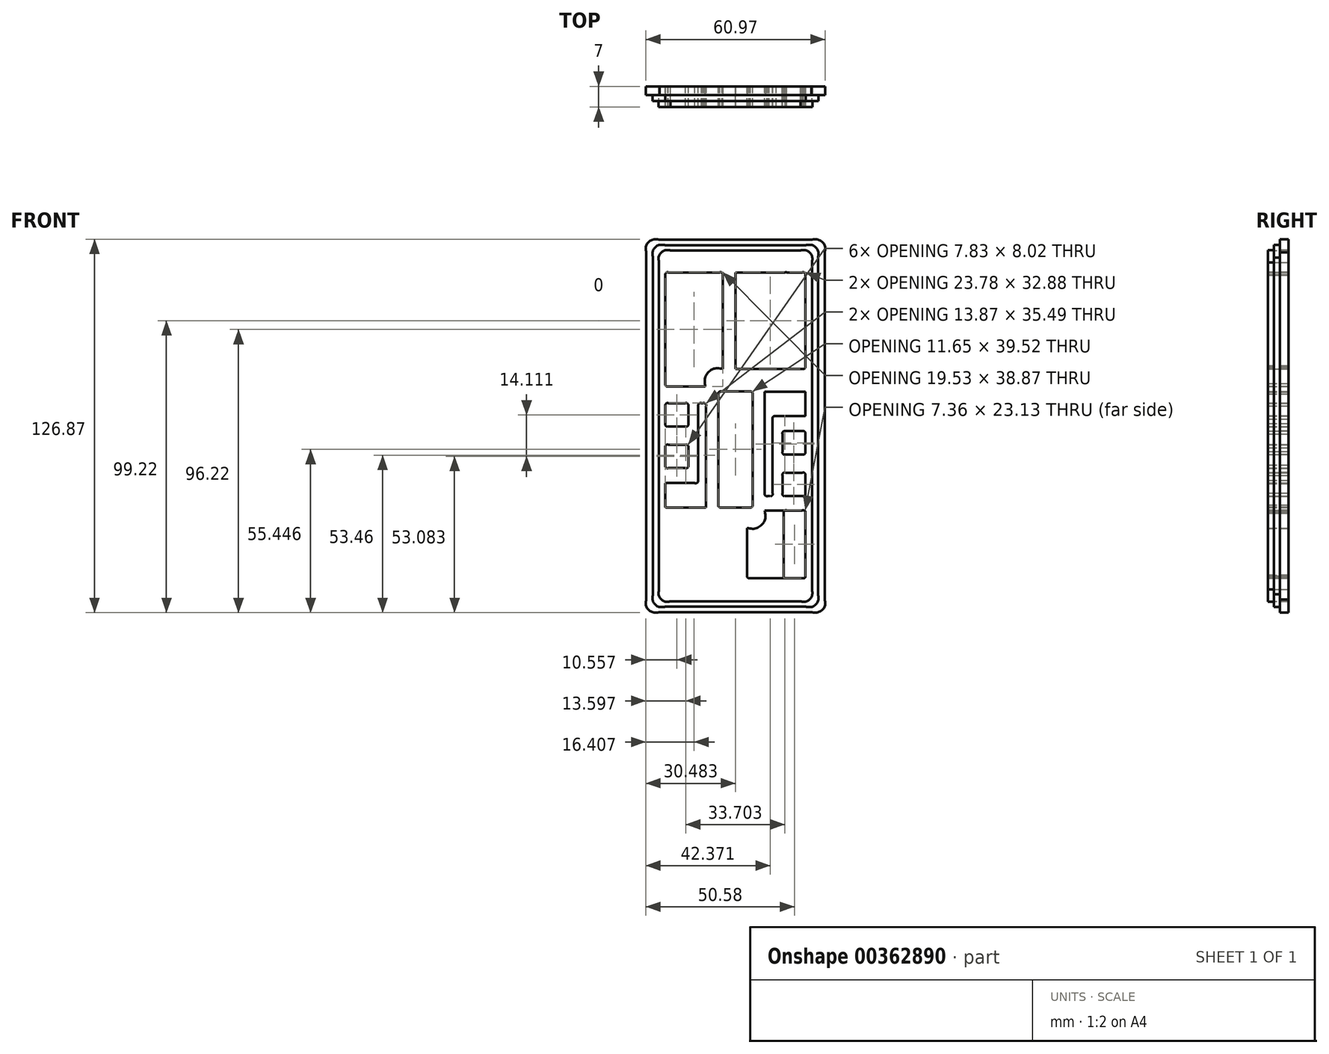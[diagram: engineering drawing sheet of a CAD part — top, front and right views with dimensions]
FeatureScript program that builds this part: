
annotation { "Feature Type Name" : "Feature", "Feature Type Description" : "" }
export const myFeature = defineFeature(function(context is Context, id is Id, definition is map)
    precondition{}
    {
        {
            var Q0;
            Q0=qCreatedBy(makeId("Front.planeOp"),FACE);
            var sketch = newSketch(context, id + "F0", { "sketchPlane" : qUnion([Q0])});
            skFitSpline(sketch, "E0", {"points": [v(-9.5, 11.52) * mm, v(-9.5, 9.28) * mm, v(-11.26, 7.48) * mm, v(-13.43, 7.48) * mm]});
            skFitSpline(sketch, "E1", {"points": [v(-57.55, 7.48) * mm, v(-59.72, 7.48) * mm, v(-61.47, 9.28) * mm, v(-61.47, 11.52) * mm]});
            skLineSegment(sketch, "E2", {"start": v(-13.43, 7.48) * mm, "end": v(-57.55, 7.48) * mm});
            skLineSegment(sketch, "E3", {"start": v(-57.55, 7.48) * mm, "end": v(-13.43, 7.48) * mm});
            skFitSpline(sketch, "E4", {"points": [v(-61.47, 122.72) * mm, v(-61.47, 124.95) * mm, v(-59.72, 126.76) * mm, v(-57.55, 126.76) * mm]});
            skLineSegment(sketch, "E5", {"start": v(-61.47, 11.52) * mm, "end": v(-61.47, 122.72) * mm});
            skLineSegment(sketch, "E6", {"start": v(-61.47, 122.72) * mm, "end": v(-61.47, 11.52) * mm});
            skFitSpline(sketch, "E7", {"points": [v(-13.43, 126.76) * mm, v(-11.26, 126.76) * mm, v(-9.5, 124.95) * mm, v(-9.5, 122.72) * mm]});
            skLineSegment(sketch, "E8", {"start": v(-57.55, 126.76) * mm, "end": v(-13.43, 126.76) * mm});
            skLineSegment(sketch, "E9", {"start": v(-13.43, 126.76) * mm, "end": v(-57.55, 126.76) * mm});
            skFitSpline(sketch, "E10", {"points": [v(-7.42, 9.85) * mm, v(-7.42, 7.55) * mm, v(-9.32, 5.69) * mm, v(-11.66, 5.69) * mm]});
            skLineSegment(sketch, "E11", {"start": v(-9.5, 122.72) * mm, "end": v(-9.5, 11.52) * mm});
            skLineSegment(sketch, "E12", {"start": v(-9.5, 11.52) * mm, "end": v(-9.5, 122.72) * mm});
            skFitSpline(sketch, "E13", {"points": [v(-59.31, 5.69) * mm, v(-61.65, 5.69) * mm, v(-63.55, 7.55) * mm, v(-63.55, 9.85) * mm]});
            skLineSegment(sketch, "E14", {"start": v(-11.66, 5.69) * mm, "end": v(-59.31, 5.69) * mm});
            skLineSegment(sketch, "E15", {"start": v(-59.31, 5.69) * mm, "end": v(-11.66, 5.69) * mm});
            skFitSpline(sketch, "E16", {"points": [v(-63.55, 124.38) * mm, v(-63.55, 126.68) * mm, v(-61.65, 128.54) * mm, v(-59.31, 128.54) * mm]});
            skLineSegment(sketch, "E17", {"start": v(-63.55, 9.85) * mm, "end": v(-63.55, 124.38) * mm});
            skLineSegment(sketch, "E18", {"start": v(-63.55, 124.38) * mm, "end": v(-63.55, 9.85) * mm});
            skFitSpline(sketch, "E19", {"points": [v(-11.66, 128.54) * mm, v(-9.32, 128.54) * mm, v(-7.42, 126.68) * mm, v(-7.42, 124.38) * mm]});
            skLineSegment(sketch, "E20", {"start": v(-59.31, 128.54) * mm, "end": v(-11.66, 128.54) * mm});
            skLineSegment(sketch, "E21", {"start": v(-11.66, 128.54) * mm, "end": v(-59.31, 128.54) * mm});
            skFitSpline(sketch, "E22", {"points": [v(-5.17, 8.13) * mm, v(-5.17, 5.76) * mm, v(-7.23, 3.84) * mm, v(-9.76, 3.84) * mm]});
            skLineSegment(sketch, "E23", {"start": v(-7.42, 124.38) * mm, "end": v(-7.42, 9.85) * mm});
            skLineSegment(sketch, "E24", {"start": v(-7.42, 9.85) * mm, "end": v(-7.42, 124.38) * mm});
            skFitSpline(sketch, "E25", {"points": [v(-61.22, 3.84) * mm, v(-63.75, 3.84) * mm, v(-65.8, 5.76) * mm, v(-65.8, 8.13) * mm]});
            skLineSegment(sketch, "E26", {"start": v(-9.76, 3.84) * mm, "end": v(-61.22, 3.84) * mm});
            skLineSegment(sketch, "E27", {"start": v(-61.22, 3.84) * mm, "end": v(-9.76, 3.84) * mm});
            skFitSpline(sketch, "E28", {"points": [v(-65.8, 126.1) * mm, v(-65.8, 128.47) * mm, v(-63.75, 130.39) * mm, v(-61.22, 130.39) * mm]});
            skLineSegment(sketch, "E29", {"start": v(-65.8, 8.13) * mm, "end": v(-65.8, 126.1) * mm});
            skLineSegment(sketch, "E30", {"start": v(-65.8, 126.1) * mm, "end": v(-65.8, 8.13) * mm});
            skFitSpline(sketch, "E31", {"points": [v(-9.76, 130.39) * mm, v(-7.23, 130.39) * mm, v(-5.17, 128.47) * mm, v(-5.17, 126.1) * mm]});
            skLineSegment(sketch, "E32", {"start": v(-61.22, 130.39) * mm, "end": v(-9.76, 130.39) * mm});
            skLineSegment(sketch, "E33", {"start": v(-9.76, 130.39) * mm, "end": v(-61.22, 130.39) * mm});
            skFitSpline(sketch, "E34", {"points": [v(66.14, 8.13) * mm, v(66.14, 5.76) * mm, v(64.1, 3.84) * mm, v(61.56, 3.84) * mm]});
            skLineSegment(sketch, "E35", {"start": v(-5.17, 126.1) * mm, "end": v(-5.17, 8.13) * mm});
            skLineSegment(sketch, "E36", {"start": v(-5.17, 8.13) * mm, "end": v(-5.17, 126.1) * mm});
            skFitSpline(sketch, "E37", {"points": [v(10.1, 3.84) * mm, v(7.57, 3.84) * mm, v(5.52, 5.76) * mm, v(5.52, 8.13) * mm]});
            skLineSegment(sketch, "E38", {"start": v(61.56, 3.84) * mm, "end": v(10.1, 3.84) * mm});
            skLineSegment(sketch, "E39", {"start": v(10.1, 3.84) * mm, "end": v(61.56, 3.84) * mm});
            skFitSpline(sketch, "E40", {"points": [v(5.52, 126.1) * mm, v(5.52, 128.47) * mm, v(7.57, 130.39) * mm, v(10.1, 130.39) * mm]});
            skLineSegment(sketch, "E41", {"start": v(5.52, 8.13) * mm, "end": v(5.52, 126.1) * mm});
            skLineSegment(sketch, "E42", {"start": v(5.52, 126.1) * mm, "end": v(5.52, 8.13) * mm});
            skFitSpline(sketch, "E43", {"points": [v(61.56, 130.39) * mm, v(64.1, 130.39) * mm, v(66.14, 128.47) * mm, v(66.14, 126.1) * mm]});
            skLineSegment(sketch, "E44", {"start": v(10.1, 130.39) * mm, "end": v(61.56, 130.39) * mm});
            skLineSegment(sketch, "E45", {"start": v(61.56, 130.39) * mm, "end": v(10.1, 130.39) * mm});
            skLineSegment(sketch, "E46", {"start": v(66.14, 126.1) * mm, "end": v(66.14, 8.13) * mm});
            skLineSegment(sketch, "E47", {"start": v(66.14, 8.13) * mm, "end": v(66.14, 126.1) * mm});
            skLineSegment(sketch, "E48", {"start": v(-35.49, 39.4) * mm, "end": v(-35.49, 7.48) * mm});
            skFitSpline(sketch, "E49", {"points": [v(-29.7, 40.28) * mm, v(-29.7, 39.8) * mm, v(-30.25, 39.4) * mm, v(-30.93, 39.4) * mm]});
            skLineSegment(sketch, "E50", {"start": v(-35.49, 126.48) * mm, "end": v(-35.49, 78.85) * mm});
            skFitSpline(sketch, "E51", {"points": [v(-40.04, 39.4) * mm, v(-40.72, 39.4) * mm, v(-41.27, 39.8) * mm, v(-41.27, 40.28) * mm]});
            skLineSegment(sketch, "E52", {"start": v(-30.93, 39.4) * mm, "end": v(-40.04, 39.4) * mm});
            skLineSegment(sketch, "E53", {"start": v(-40.04, 39.4) * mm, "end": v(-30.93, 39.4) * mm});
            skFitSpline(sketch, "E54", {"points": [v(-41.27, 77.97) * mm, v(-41.27, 78.46) * mm, v(-40.72, 78.85) * mm, v(-40.04, 78.85) * mm]});
            skLineSegment(sketch, "E55", {"start": v(-41.27, 40.28) * mm, "end": v(-41.27, 77.97) * mm});
            skLineSegment(sketch, "E56", {"start": v(-41.27, 77.97) * mm, "end": v(-41.27, 40.28) * mm});
            skFitSpline(sketch, "E57", {"points": [v(-30.93, 78.85) * mm, v(-30.25, 78.85) * mm, v(-29.7, 78.46) * mm, v(-29.7, 77.97) * mm]});
            skLineSegment(sketch, "E58", {"start": v(-40.04, 78.85) * mm, "end": v(-30.93, 78.85) * mm});
            skLineSegment(sketch, "E59", {"start": v(-30.93, 78.85) * mm, "end": v(-40.04, 78.85) * mm});
            skLineSegment(sketch, "E60", {"start": v(-29.7, 77.97) * mm, "end": v(-29.7, 40.28) * mm});
            skLineSegment(sketch, "E61", {"start": v(-29.7, 40.28) * mm, "end": v(-29.7, 77.97) * mm});
            skFitSpline(sketch, "E62", {"points": [v(-25.57, 78.55) * mm, v(-25.57, 78.65) * mm, v(-25.2, 78.72) * mm, v(-24.77, 78.72) * mm]});
            skLineSegment(sketch, "E63", {"start": v(-25.57, 72.08) * mm, "end": v(-25.57, 78.55) * mm});
            skLineSegment(sketch, "E64", {"start": v(-25.57, 78.55) * mm, "end": v(-25.57, 72.08) * mm});
            skFitSpline(sketch, "E65", {"points": [v(-12.55, 78.72) * mm, v(-12.1, 78.72) * mm, v(-11.75, 78.65) * mm, v(-11.75, 78.55) * mm]});
            skLineSegment(sketch, "E66", {"start": v(-24.77, 78.72) * mm, "end": v(-12.55, 78.72) * mm});
            skLineSegment(sketch, "E67", {"start": v(-12.55, 78.72) * mm, "end": v(-24.77, 78.72) * mm});
            skFitSpline(sketch, "E68", {"points": [v(-11.75, 70.6) * mm, v(-11.75, 70.51) * mm, v(-12.1, 70.43) * mm, v(-12.55, 70.43) * mm]});
            skLineSegment(sketch, "E69", {"start": v(-11.75, 78.55) * mm, "end": v(-11.75, 70.6) * mm});
            skLineSegment(sketch, "E70", {"start": v(-11.75, 70.6) * mm, "end": v(-11.75, 78.55) * mm});
            skFitSpline(sketch, "E71", {"points": [v(-21.68, 70.43) * mm, v(-22.33, 70.43) * mm, v(-22.86, 69.99) * mm, v(-22.86, 69.44) * mm]});
            skLineSegment(sketch, "E72", {"start": v(-12.55, 70.43) * mm, "end": v(-19.74, 70.43) * mm});
            skLineSegment(sketch, "E73", {"start": v(-19.74, 70.43) * mm, "end": v(-21.68, 70.43) * mm});
            skLineSegment(sketch, "E74", {"start": v(-21.68, 70.43) * mm, "end": v(-12.55, 70.43) * mm});
            skFitSpline(sketch, "E75", {"points": [v(-22.86, 44.26) * mm, v(-22.86, 43.72) * mm, v(-23.39, 43.27) * mm, v(-24.04, 43.27) * mm]});
            skLineSegment(sketch, "E76", {"start": v(-22.86, 69.44) * mm, "end": v(-22.86, 59.26) * mm});
            skLineSegment(sketch, "E77", {"start": v(-22.86, 59.26) * mm, "end": v(-22.86, 56.91) * mm});
            skLineSegment(sketch, "E78", {"start": v(-22.86, 56.91) * mm, "end": v(-22.86, 44.26) * mm});
            skLineSegment(sketch, "E79", {"start": v(-22.86, 44.26) * mm, "end": v(-22.86, 69.44) * mm});
            skFitSpline(sketch, "E80", {"points": [v(-24.39, 43.27) * mm, v(-25.04, 43.27) * mm, v(-25.57, 43.72) * mm, v(-25.57, 44.26) * mm]});
            skLineSegment(sketch, "E81", {"start": v(-24.04, 43.27) * mm, "end": v(-24.39, 43.27) * mm});
            skLineSegment(sketch, "E82", {"start": v(-24.39, 43.27) * mm, "end": v(-24.04, 43.27) * mm});
            skFitSpline(sketch, "E83", {"points": [v(-11.75, 58.38) * mm, v(-11.75, 57.83) * mm, v(-12.2, 57.38) * mm, v(-12.75, 57.38) * mm]});
            skLineSegment(sketch, "E84", {"start": v(-25.57, 44.26) * mm, "end": v(-25.57, 63.14) * mm});
            skLineSegment(sketch, "E85", {"start": v(-25.57, 63.14) * mm, "end": v(-25.57, 72.08) * mm});
            skLineSegment(sketch, "E86", {"start": v(-25.57, 72.08) * mm, "end": v(-25.57, 44.26) * mm});
            skFitSpline(sketch, "E87", {"points": [v(-18.5, 57.38) * mm, v(-19.06, 57.38) * mm, v(-19.5, 57.83) * mm, v(-19.5, 58.38) * mm]});
            skLineSegment(sketch, "E88", {"start": v(-12.75, 57.38) * mm, "end": v(-18.5, 57.38) * mm});
            skLineSegment(sketch, "E89", {"start": v(-18.5, 57.38) * mm, "end": v(-12.75, 57.38) * mm});
            skFitSpline(sketch, "E90", {"points": [v(-19.5, 64.34) * mm, v(-19.5, 64.9) * mm, v(-19.06, 65.34) * mm, v(-18.5, 65.34) * mm]});
            skLineSegment(sketch, "E91", {"start": v(-19.5, 58.38) * mm, "end": v(-19.5, 64.34) * mm});
            skLineSegment(sketch, "E92", {"start": v(-19.5, 64.34) * mm, "end": v(-19.5, 58.38) * mm});
            skFitSpline(sketch, "E93", {"points": [v(-12.75, 65.34) * mm, v(-12.2, 65.34) * mm, v(-11.75, 64.9) * mm, v(-11.75, 64.34) * mm]});
            skLineSegment(sketch, "E94", {"start": v(-18.5, 65.34) * mm, "end": v(-12.75, 65.34) * mm});
            skLineSegment(sketch, "E95", {"start": v(-12.75, 65.34) * mm, "end": v(-18.5, 65.34) * mm});
            skFitSpline(sketch, "E96", {"points": [v(-11.75, 44.27) * mm, v(-11.75, 43.72) * mm, v(-12.2, 43.27) * mm, v(-12.75, 43.27) * mm]});
            skLineSegment(sketch, "E97", {"start": v(-11.75, 64.34) * mm, "end": v(-11.75, 58.38) * mm});
            skLineSegment(sketch, "E98", {"start": v(-11.75, 58.38) * mm, "end": v(-11.75, 64.34) * mm});
            skFitSpline(sketch, "E99", {"points": [v(-18.5, 43.27) * mm, v(-19.06, 43.27) * mm, v(-19.5, 43.72) * mm, v(-19.5, 44.27) * mm]});
            skLineSegment(sketch, "E100", {"start": v(-12.75, 43.27) * mm, "end": v(-18.5, 43.27) * mm});
            skLineSegment(sketch, "E101", {"start": v(-18.5, 43.27) * mm, "end": v(-12.75, 43.27) * mm});
            skFitSpline(sketch, "E102", {"points": [v(-19.5, 50.23) * mm, v(-19.5, 50.78) * mm, v(-19.06, 51.23) * mm, v(-18.5, 51.23) * mm]});
            skLineSegment(sketch, "E103", {"start": v(-19.5, 44.27) * mm, "end": v(-19.5, 50.23) * mm});
            skLineSegment(sketch, "E104", {"start": v(-19.5, 50.23) * mm, "end": v(-19.5, 44.27) * mm});
            skFitSpline(sketch, "E105", {"points": [v(-12.75, 51.23) * mm, v(-12.2, 51.23) * mm, v(-11.75, 50.78) * mm, v(-11.75, 50.23) * mm]});
            skLineSegment(sketch, "E106", {"start": v(-18.5, 51.23) * mm, "end": v(-12.75, 51.23) * mm});
            skLineSegment(sketch, "E107", {"start": v(-12.75, 51.23) * mm, "end": v(-18.5, 51.23) * mm});
            skLineSegment(sketch, "E108", {"start": v(-11.75, 50.23) * mm, "end": v(-11.75, 44.27) * mm});
            skLineSegment(sketch, "E109", {"start": v(-11.75, 44.27) * mm, "end": v(-11.75, 50.23) * mm});
            skFitSpline(sketch, "E110", {"points": [v(-45.48, 39.57) * mm, v(-45.48, 39.48) * mm, v(-45.83, 39.4) * mm, v(-46.28, 39.4) * mm]});
            skLineSegment(sketch, "E111", {"start": v(-45.48, 46.04) * mm, "end": v(-45.48, 39.57) * mm});
            skLineSegment(sketch, "E112", {"start": v(-45.48, 39.57) * mm, "end": v(-45.48, 46.04) * mm});
            skFitSpline(sketch, "E113", {"points": [v(-58.5, 39.4) * mm, v(-58.94, 39.4) * mm, v(-59.3, 39.48) * mm, v(-59.3, 39.57) * mm]});
            skLineSegment(sketch, "E114", {"start": v(-46.28, 39.4) * mm, "end": v(-58.5, 39.4) * mm});
            skLineSegment(sketch, "E115", {"start": v(-58.5, 39.4) * mm, "end": v(-46.28, 39.4) * mm});
            skFitSpline(sketch, "E116", {"points": [v(-59.3, 47.51) * mm, v(-59.3, 47.61) * mm, v(-58.94, 47.69) * mm, v(-58.5, 47.69) * mm]});
            skLineSegment(sketch, "E117", {"start": v(-59.3, 39.57) * mm, "end": v(-59.3, 47.51) * mm});
            skLineSegment(sketch, "E118", {"start": v(-59.3, 47.51) * mm, "end": v(-59.3, 39.57) * mm});
            skFitSpline(sketch, "E119", {"points": [v(-49.36, 47.69) * mm, v(-48.7, 47.69) * mm, v(-48.18, 48.13) * mm, v(-48.18, 48.68) * mm]});
            skLineSegment(sketch, "E120", {"start": v(-58.5, 47.69) * mm, "end": v(-51.3, 47.69) * mm});
            skLineSegment(sketch, "E121", {"start": v(-51.3, 47.69) * mm, "end": v(-49.36, 47.69) * mm});
            skLineSegment(sketch, "E122", {"start": v(-49.36, 47.69) * mm, "end": v(-58.5, 47.69) * mm});
            skFitSpline(sketch, "E123", {"points": [v(-48.18, 73.86) * mm, v(-48.18, 74.4) * mm, v(-47.65, 74.85) * mm, v(-47, 74.85) * mm]});
            skLineSegment(sketch, "E124", {"start": v(-48.18, 48.68) * mm, "end": v(-48.18, 58.86) * mm});
            skLineSegment(sketch, "E125", {"start": v(-48.18, 58.86) * mm, "end": v(-48.18, 61.21) * mm});
            skLineSegment(sketch, "E126", {"start": v(-48.18, 61.21) * mm, "end": v(-48.18, 73.86) * mm});
            skLineSegment(sketch, "E127", {"start": v(-48.18, 73.86) * mm, "end": v(-48.18, 48.68) * mm});
            skFitSpline(sketch, "E128", {"points": [v(-46.66, 74.85) * mm, v(-46, 74.85) * mm, v(-45.48, 74.4) * mm, v(-45.48, 73.86) * mm]});
            skLineSegment(sketch, "E129", {"start": v(-47, 74.85) * mm, "end": v(-46.66, 74.85) * mm});
            skLineSegment(sketch, "E130", {"start": v(-46.66, 74.85) * mm, "end": v(-47, 74.85) * mm});
            skFitSpline(sketch, "E131", {"points": [v(-59.3, 59.74) * mm, v(-59.3, 60.3) * mm, v(-58.85, 60.74) * mm, v(-58.3, 60.74) * mm]});
            skLineSegment(sketch, "E132", {"start": v(-45.48, 73.86) * mm, "end": v(-45.48, 54.98) * mm});
            skLineSegment(sketch, "E133", {"start": v(-45.48, 54.98) * mm, "end": v(-45.48, 46.04) * mm});
            skLineSegment(sketch, "E134", {"start": v(-45.48, 46.04) * mm, "end": v(-45.48, 73.86) * mm});
            skFitSpline(sketch, "E135", {"points": [v(-52.53, 60.74) * mm, v(-51.98, 60.74) * mm, v(-51.53, 60.3) * mm, v(-51.53, 59.74) * mm]});
            skLineSegment(sketch, "E136", {"start": v(-58.3, 60.74) * mm, "end": v(-52.53, 60.74) * mm});
            skLineSegment(sketch, "E137", {"start": v(-52.53, 60.74) * mm, "end": v(-58.3, 60.74) * mm});
            skFitSpline(sketch, "E138", {"points": [v(-51.53, 53.78) * mm, v(-51.53, 53.23) * mm, v(-51.98, 52.78) * mm, v(-52.53, 52.78) * mm]});
            skLineSegment(sketch, "E139", {"start": v(-51.53, 59.74) * mm, "end": v(-51.53, 53.78) * mm});
            skLineSegment(sketch, "E140", {"start": v(-51.53, 53.78) * mm, "end": v(-51.53, 59.74) * mm});
            skFitSpline(sketch, "E141", {"points": [v(-58.3, 52.78) * mm, v(-58.85, 52.78) * mm, v(-59.3, 53.23) * mm, v(-59.3, 53.78) * mm]});
            skLineSegment(sketch, "E142", {"start": v(-52.53, 52.78) * mm, "end": v(-58.3, 52.78) * mm});
            skLineSegment(sketch, "E143", {"start": v(-58.3, 52.78) * mm, "end": v(-52.53, 52.78) * mm});
            skFitSpline(sketch, "E144", {"points": [v(-59.3, 73.85) * mm, v(-59.3, 74.4) * mm, v(-58.85, 74.85) * mm, v(-58.3, 74.85) * mm]});
            skLineSegment(sketch, "E145", {"start": v(-59.3, 53.78) * mm, "end": v(-59.3, 59.74) * mm});
            skLineSegment(sketch, "E146", {"start": v(-59.3, 59.74) * mm, "end": v(-59.3, 53.78) * mm});
            skFitSpline(sketch, "E147", {"points": [v(-52.53, 74.85) * mm, v(-51.98, 74.85) * mm, v(-51.53, 74.4) * mm, v(-51.53, 73.85) * mm]});
            skLineSegment(sketch, "E148", {"start": v(-58.3, 74.85) * mm, "end": v(-52.53, 74.85) * mm});
            skLineSegment(sketch, "E149", {"start": v(-52.53, 74.85) * mm, "end": v(-58.3, 74.85) * mm});
            skFitSpline(sketch, "E150", {"points": [v(-51.53, 67.9) * mm, v(-51.53, 67.34) * mm, v(-51.98, 66.9) * mm, v(-52.53, 66.9) * mm]});
            skLineSegment(sketch, "E151", {"start": v(-51.53, 73.85) * mm, "end": v(-51.53, 67.9) * mm});
            skLineSegment(sketch, "E152", {"start": v(-51.53, 67.9) * mm, "end": v(-51.53, 73.85) * mm});
            skFitSpline(sketch, "E153", {"points": [v(-58.3, 66.9) * mm, v(-58.85, 66.9) * mm, v(-59.3, 67.34) * mm, v(-59.3, 67.9) * mm]});
            skLineSegment(sketch, "E154", {"start": v(-52.53, 66.9) * mm, "end": v(-58.3, 66.9) * mm});
            skLineSegment(sketch, "E155", {"start": v(-58.3, 66.9) * mm, "end": v(-52.53, 66.9) * mm});
            skLineSegment(sketch, "E156", {"start": v(-59.3, 67.9) * mm, "end": v(-59.3, 73.85) * mm});
            skLineSegment(sketch, "E157", {"start": v(-59.3, 73.85) * mm, "end": v(-59.3, 67.9) * mm});
            skFitSpline(sketch, "E158", {"points": [v(-39.83, 118.3) * mm, v(-39.83, 118.86) * mm, v(-40.28, 119.3) * mm, v(-40.84, 119.3) * mm]});
            skLineSegment(sketch, "E159", {"start": v(-39.83, 92.85) * mm, "end": v(-39.83, 118.3) * mm});
            skLineSegment(sketch, "E160", {"start": v(-39.83, 118.3) * mm, "end": v(-39.83, 92.85) * mm});
            skFitSpline(sketch, "E161", {"points": [v(-58.28, 119.3) * mm, v(-58.84, 119.3) * mm, v(-59.3, 118.86) * mm, v(-59.3, 118.3) * mm]});
            skLineSegment(sketch, "E162", {"start": v(-40.84, 119.3) * mm, "end": v(-58.28, 119.3) * mm});
            skLineSegment(sketch, "E163", {"start": v(-58.28, 119.3) * mm, "end": v(-40.84, 119.3) * mm});
            skFitSpline(sketch, "E164", {"points": [v(-59.3, 81.5) * mm, v(-59.3, 80.95) * mm, v(-58.84, 80.5) * mm, v(-58.28, 80.5) * mm]});
            skLineSegment(sketch, "E165", {"start": v(-59.3, 118.3) * mm, "end": v(-59.3, 81.5) * mm});
            skLineSegment(sketch, "E166", {"start": v(-59.3, 81.5) * mm, "end": v(-59.3, 118.3) * mm});
            skFitSpline(sketch, "E167", {"points": [v(-45.71, 80.5) * mm, v(-45.71, 83.81) * mm, v(-43.08, 86.5) * mm, v(-39.83, 86.5) * mm]});
            skLineSegment(sketch, "E168", {"start": v(-58.28, 80.5) * mm, "end": v(-51.74, 80.5) * mm});
            skLineSegment(sketch, "E169", {"start": v(-51.74, 80.5) * mm, "end": v(-45.71, 80.5) * mm});
            skLineSegment(sketch, "E170", {"start": v(-45.71, 80.5) * mm, "end": v(-58.28, 80.5) * mm});
            skLineSegment(sketch, "E171", {"start": v(-39.83, 86.5) * mm, "end": v(-39.83, 92.85) * mm});
            skLineSegment(sketch, "E172", {"start": v(-39.83, 92.85) * mm, "end": v(-39.83, 86.5) * mm});
            skFitSpline(sketch, "E173", {"points": [v(-31.53, 16.36) * mm, v(-31.53, 15.8) * mm, v(-31.04, 15.36) * mm, v(-30.44, 15.36) * mm]});
            skLineSegment(sketch, "E174", {"start": v(-31.53, 23) * mm, "end": v(-31.53, 16.36) * mm});
            skLineSegment(sketch, "E175", {"start": v(-31.53, 16.36) * mm, "end": v(-31.53, 23) * mm});
            skFitSpline(sketch, "E176", {"points": [v(-12.84, 15.36) * mm, v(-12.24, 15.36) * mm, v(-11.75, 15.8) * mm, v(-11.75, 16.36) * mm]});
            skLineSegment(sketch, "E177", {"start": v(-30.44, 15.36) * mm, "end": v(-12.84, 15.36) * mm});
            skLineSegment(sketch, "E178", {"start": v(-12.84, 15.36) * mm, "end": v(-30.44, 15.36) * mm});
            skFitSpline(sketch, "E179", {"points": [v(-11.75, 37.4) * mm, v(-11.75, 37.96) * mm, v(-12.24, 38.4) * mm, v(-12.84, 38.4) * mm]});
            skLineSegment(sketch, "E180", {"start": v(-11.75, 16.36) * mm, "end": v(-11.75, 37.4) * mm});
            skLineSegment(sketch, "E181", {"start": v(-11.75, 37.4) * mm, "end": v(-11.75, 16.36) * mm});
            skFitSpline(sketch, "E182", {"points": [v(-25.53, 38.4) * mm, v(-25.53, 35.1) * mm, v(-28.22, 32.4) * mm, v(-31.53, 32.4) * mm]});
            skLineSegment(sketch, "E183", {"start": v(-12.84, 38.4) * mm, "end": v(-19.6, 38.4) * mm});
            skLineSegment(sketch, "E184", {"start": v(-19.6, 38.4) * mm, "end": v(-25.53, 38.4) * mm});
            skLineSegment(sketch, "E185", {"start": v(-25.53, 38.4) * mm, "end": v(-12.84, 38.4) * mm});
            skLineSegment(sketch, "E186", {"start": v(-31.53, 32.4) * mm, "end": v(-31.53, 23) * mm});
            skLineSegment(sketch, "E187", {"start": v(-31.53, 23) * mm, "end": v(-31.53, 32.4) * mm});
            skFitSpline(sketch, "E188", {"points": [v(-57.9, 15.36) * mm, v(-58.67, 15.36) * mm, v(-59.3, 15.83) * mm, v(-59.3, 16.42) * mm]});
            skLineSegment(sketch, "E189", {"start": v(-35.49, 15.36) * mm, "end": v(-57.9, 15.36) * mm});
            skFitSpline(sketch, "E190", {"points": [v(-59.3, 31.34) * mm, v(-59.3, 31.93) * mm, v(-58.67, 32.4) * mm, v(-57.9, 32.4) * mm]});
            skLineSegment(sketch, "E191", {"start": v(-59.3, 16.42) * mm, "end": v(-59.3, 31.34) * mm});
            skLineSegment(sketch, "E192", {"start": v(-57.9, 32.4) * mm, "end": v(-35.49, 32.4) * mm});
            skFitSpline(sketch, "E193", {"points": [v(-12.75, 86.5) * mm, v(-12.2, 86.5) * mm, v(-11.75, 86.95) * mm, v(-11.75, 87.5) * mm]});
            skLineSegment(sketch, "E194", {"start": v(-35.49, 86.5) * mm, "end": v(-12.75, 86.5) * mm});
            skFitSpline(sketch, "E195", {"points": [v(-11.75, 118.3) * mm, v(-11.75, 118.86) * mm, v(-12.2, 119.3) * mm, v(-12.75, 119.3) * mm]});
            skLineSegment(sketch, "E196", {"start": v(-11.75, 87.5) * mm, "end": v(-11.75, 118.3) * mm});
            skFitSpline(sketch, "E197", {"points": [v(-9.5, -123.06) * mm, v(-9.5, -125.3) * mm, v(-11.26, -127.1) * mm, v(-13.43, -127.1) * mm]});
            skLineSegment(sketch, "E198", {"start": v(-12.75, 119.3) * mm, "end": v(-35.49, 119.3) * mm});
            skFitSpline(sketch, "E199", {"points": [v(-57.55, -127.1) * mm, v(-59.72, -127.1) * mm, v(-61.47, -125.3) * mm, v(-61.47, -123.06) * mm]});
            skLineSegment(sketch, "E200", {"start": v(-13.43, -127.1) * mm, "end": v(-57.55, -127.1) * mm});
            skLineSegment(sketch, "E201", {"start": v(-57.55, -127.1) * mm, "end": v(-13.43, -127.1) * mm});
            skFitSpline(sketch, "E202", {"points": [v(-61.47, -11.86) * mm, v(-61.47, -9.63) * mm, v(-59.72, -7.82) * mm, v(-57.55, -7.82) * mm]});
            skLineSegment(sketch, "E203", {"start": v(-61.47, -123.06) * mm, "end": v(-61.47, -11.86) * mm});
            skLineSegment(sketch, "E204", {"start": v(-61.47, -11.86) * mm, "end": v(-61.47, -123.06) * mm});
            skFitSpline(sketch, "E205", {"points": [v(-13.43, -7.82) * mm, v(-11.26, -7.82) * mm, v(-9.5, -9.63) * mm, v(-9.5, -11.86) * mm]});
            skLineSegment(sketch, "E206", {"start": v(-57.55, -7.82) * mm, "end": v(-13.43, -7.82) * mm});
            skLineSegment(sketch, "E207", {"start": v(-13.43, -7.82) * mm, "end": v(-57.55, -7.82) * mm});
            skLineSegment(sketch, "E208", {"start": v(-9.5, -11.86) * mm, "end": v(-9.5, -123.06) * mm});
            skLineSegment(sketch, "E209", {"start": v(-9.5, -123.06) * mm, "end": v(-9.5, -11.86) * mm});
            skLineSegment(sketch, "E210", {"start": v(-35.49, -95.18) * mm, "end": v(-35.49, -127.1) * mm});
            skFitSpline(sketch, "E211", {"points": [v(-29.7, -94.3) * mm, v(-29.7, -94.78) * mm, v(-30.25, -95.18) * mm, v(-30.93, -95.18) * mm]});
            skLineSegment(sketch, "E212", {"start": v(-35.49, -8.1) * mm, "end": v(-35.49, -55.72) * mm});
            skFitSpline(sketch, "E213", {"points": [v(-40.04, -95.18) * mm, v(-40.72, -95.18) * mm, v(-41.27, -94.78) * mm, v(-41.27, -94.3) * mm]});
            skLineSegment(sketch, "E214", {"start": v(-30.93, -95.18) * mm, "end": v(-40.04, -95.18) * mm});
            skLineSegment(sketch, "E215", {"start": v(-40.04, -95.18) * mm, "end": v(-30.93, -95.18) * mm});
            skFitSpline(sketch, "E216", {"points": [v(-41.27, -56.6) * mm, v(-41.27, -56.12) * mm, v(-40.72, -55.72) * mm, v(-40.04, -55.72) * mm]});
            skLineSegment(sketch, "E217", {"start": v(-41.27, -94.3) * mm, "end": v(-41.27, -56.6) * mm});
            skLineSegment(sketch, "E218", {"start": v(-41.27, -56.6) * mm, "end": v(-41.27, -94.3) * mm});
            skFitSpline(sketch, "E219", {"points": [v(-30.93, -55.72) * mm, v(-30.25, -55.72) * mm, v(-29.7, -56.12) * mm, v(-29.7, -56.6) * mm]});
            skLineSegment(sketch, "E220", {"start": v(-40.04, -55.72) * mm, "end": v(-30.93, -55.72) * mm});
            skLineSegment(sketch, "E221", {"start": v(-30.93, -55.72) * mm, "end": v(-40.04, -55.72) * mm});
            skLineSegment(sketch, "E222", {"start": v(-29.7, -56.6) * mm, "end": v(-29.7, -94.3) * mm});
            skLineSegment(sketch, "E223", {"start": v(-29.7, -94.3) * mm, "end": v(-29.7, -56.6) * mm});
            skFitSpline(sketch, "E224", {"points": [v(-25.57, -56.03) * mm, v(-25.57, -55.93) * mm, v(-25.2, -55.85) * mm, v(-24.77, -55.85) * mm]});
            skLineSegment(sketch, "E225", {"start": v(-25.57, -62.5) * mm, "end": v(-25.57, -56.03) * mm});
            skLineSegment(sketch, "E226", {"start": v(-25.57, -56.03) * mm, "end": v(-25.57, -62.5) * mm});
            skFitSpline(sketch, "E227", {"points": [v(-12.55, -55.85) * mm, v(-12.1, -55.85) * mm, v(-11.75, -55.93) * mm, v(-11.75, -56.03) * mm]});
            skLineSegment(sketch, "E228", {"start": v(-24.77, -55.85) * mm, "end": v(-12.55, -55.85) * mm});
            skLineSegment(sketch, "E229", {"start": v(-12.55, -55.85) * mm, "end": v(-24.77, -55.85) * mm});
            skFitSpline(sketch, "E230", {"points": [v(-11.75, -63.97) * mm, v(-11.75, -64.07) * mm, v(-12.1, -64.14) * mm, v(-12.55, -64.14) * mm]});
            skLineSegment(sketch, "E231", {"start": v(-11.75, -56.03) * mm, "end": v(-11.75, -63.97) * mm});
            skLineSegment(sketch, "E232", {"start": v(-11.75, -63.97) * mm, "end": v(-11.75, -56.03) * mm});
            skFitSpline(sketch, "E233", {"points": [v(-21.68, -64.14) * mm, v(-22.33, -64.14) * mm, v(-22.86, -64.59) * mm, v(-22.86, -65.14) * mm]});
            skLineSegment(sketch, "E234", {"start": v(-12.55, -64.14) * mm, "end": v(-19.74, -64.14) * mm});
            skLineSegment(sketch, "E235", {"start": v(-19.74, -64.14) * mm, "end": v(-21.68, -64.14) * mm});
            skLineSegment(sketch, "E236", {"start": v(-21.68, -64.14) * mm, "end": v(-12.55, -64.14) * mm});
            skFitSpline(sketch, "E237", {"points": [v(-22.86, -90.31) * mm, v(-22.86, -90.86) * mm, v(-23.39, -91.3) * mm, v(-24.04, -91.3) * mm]});
            skLineSegment(sketch, "E238", {"start": v(-22.86, -65.14) * mm, "end": v(-22.86, -75.32) * mm});
            skLineSegment(sketch, "E239", {"start": v(-22.86, -75.32) * mm, "end": v(-22.86, -77.67) * mm});
            skLineSegment(sketch, "E240", {"start": v(-22.86, -77.67) * mm, "end": v(-22.86, -90.31) * mm});
            skLineSegment(sketch, "E241", {"start": v(-22.86, -90.31) * mm, "end": v(-22.86, -65.14) * mm});
            skFitSpline(sketch, "E242", {"points": [v(-24.39, -91.3) * mm, v(-25.04, -91.3) * mm, v(-25.57, -90.86) * mm, v(-25.57, -90.31) * mm]});
            skLineSegment(sketch, "E243", {"start": v(-24.04, -91.3) * mm, "end": v(-24.39, -91.3) * mm});
            skLineSegment(sketch, "E244", {"start": v(-24.39, -91.3) * mm, "end": v(-24.04, -91.3) * mm});
            skFitSpline(sketch, "E245", {"points": [v(-11.75, -76.2) * mm, v(-11.75, -76.75) * mm, v(-12.2, -77.2) * mm, v(-12.75, -77.2) * mm]});
            skLineSegment(sketch, "E246", {"start": v(-25.57, -90.31) * mm, "end": v(-25.57, -71.43) * mm});
            skLineSegment(sketch, "E247", {"start": v(-25.57, -71.43) * mm, "end": v(-25.57, -62.5) * mm});
            skLineSegment(sketch, "E248", {"start": v(-25.57, -62.5) * mm, "end": v(-25.57, -90.31) * mm});
            skFitSpline(sketch, "E249", {"points": [v(-18.5, -77.2) * mm, v(-19.06, -77.2) * mm, v(-19.5, -76.75) * mm, v(-19.5, -76.2) * mm]});
            skLineSegment(sketch, "E250", {"start": v(-12.75, -77.2) * mm, "end": v(-18.5, -77.2) * mm});
            skLineSegment(sketch, "E251", {"start": v(-18.5, -77.2) * mm, "end": v(-12.75, -77.2) * mm});
            skFitSpline(sketch, "E252", {"points": [v(-19.5, -70.24) * mm, v(-19.5, -69.69) * mm, v(-19.06, -69.24) * mm, v(-18.5, -69.24) * mm]});
            skLineSegment(sketch, "E253", {"start": v(-19.5, -76.2) * mm, "end": v(-19.5, -70.24) * mm});
            skLineSegment(sketch, "E254", {"start": v(-19.5, -70.24) * mm, "end": v(-19.5, -76.2) * mm});
            skFitSpline(sketch, "E255", {"points": [v(-12.75, -69.24) * mm, v(-12.2, -69.24) * mm, v(-11.75, -69.69) * mm, v(-11.75, -70.24) * mm]});
            skLineSegment(sketch, "E256", {"start": v(-18.5, -69.24) * mm, "end": v(-12.75, -69.24) * mm});
            skLineSegment(sketch, "E257", {"start": v(-12.75, -69.24) * mm, "end": v(-18.5, -69.24) * mm});
            skFitSpline(sketch, "E258", {"points": [v(-11.75, -90.3) * mm, v(-11.75, -90.86) * mm, v(-12.2, -91.3) * mm, v(-12.75, -91.3) * mm]});
            skLineSegment(sketch, "E259", {"start": v(-11.75, -70.24) * mm, "end": v(-11.75, -76.2) * mm});
            skLineSegment(sketch, "E260", {"start": v(-11.75, -76.2) * mm, "end": v(-11.75, -70.24) * mm});
            skFitSpline(sketch, "E261", {"points": [v(-18.5, -91.3) * mm, v(-19.06, -91.3) * mm, v(-19.5, -90.86) * mm, v(-19.5, -90.3) * mm]});
            skLineSegment(sketch, "E262", {"start": v(-12.75, -91.3) * mm, "end": v(-18.5, -91.3) * mm});
            skLineSegment(sketch, "E263", {"start": v(-18.5, -91.3) * mm, "end": v(-12.75, -91.3) * mm});
            skFitSpline(sketch, "E264", {"points": [v(-19.5, -84.35) * mm, v(-19.5, -83.8) * mm, v(-19.06, -83.35) * mm, v(-18.5, -83.35) * mm]});
            skLineSegment(sketch, "E265", {"start": v(-19.5, -90.3) * mm, "end": v(-19.5, -84.35) * mm});
            skLineSegment(sketch, "E266", {"start": v(-19.5, -84.35) * mm, "end": v(-19.5, -90.3) * mm});
            skFitSpline(sketch, "E267", {"points": [v(-12.75, -83.35) * mm, v(-12.2, -83.35) * mm, v(-11.75, -83.8) * mm, v(-11.75, -84.35) * mm]});
            skLineSegment(sketch, "E268", {"start": v(-18.5, -83.35) * mm, "end": v(-12.75, -83.35) * mm});
            skLineSegment(sketch, "E269", {"start": v(-12.75, -83.35) * mm, "end": v(-18.5, -83.35) * mm});
            skLineSegment(sketch, "E270", {"start": v(-11.75, -84.35) * mm, "end": v(-11.75, -90.3) * mm});
            skLineSegment(sketch, "E271", {"start": v(-11.75, -90.3) * mm, "end": v(-11.75, -84.35) * mm});
            skFitSpline(sketch, "E272", {"points": [v(-45.48, -95) * mm, v(-45.48, -95.1) * mm, v(-45.83, -95.18) * mm, v(-46.28, -95.18) * mm]});
            skLineSegment(sketch, "E273", {"start": v(-45.48, -88.54) * mm, "end": v(-45.48, -95) * mm});
            skLineSegment(sketch, "E274", {"start": v(-45.48, -95) * mm, "end": v(-45.48, -88.54) * mm});
            skFitSpline(sketch, "E275", {"points": [v(-58.5, -95.18) * mm, v(-58.94, -95.18) * mm, v(-59.3, -95.1) * mm, v(-59.3, -95) * mm]});
            skLineSegment(sketch, "E276", {"start": v(-46.28, -95.18) * mm, "end": v(-58.5, -95.18) * mm});
            skLineSegment(sketch, "E277", {"start": v(-58.5, -95.18) * mm, "end": v(-46.28, -95.18) * mm});
            skFitSpline(sketch, "E278", {"points": [v(-59.3, -87.06) * mm, v(-59.3, -86.97) * mm, v(-58.94, -86.89) * mm, v(-58.5, -86.89) * mm]});
            skLineSegment(sketch, "E279", {"start": v(-59.3, -95) * mm, "end": v(-59.3, -87.06) * mm});
            skLineSegment(sketch, "E280", {"start": v(-59.3, -87.06) * mm, "end": v(-59.3, -95) * mm});
            skFitSpline(sketch, "E281", {"points": [v(-49.36, -86.89) * mm, v(-48.7, -86.89) * mm, v(-48.18, -86.44) * mm, v(-48.18, -85.9) * mm]});
            skLineSegment(sketch, "E282", {"start": v(-58.5, -86.89) * mm, "end": v(-51.3, -86.89) * mm});
            skLineSegment(sketch, "E283", {"start": v(-51.3, -86.89) * mm, "end": v(-49.36, -86.89) * mm});
            skLineSegment(sketch, "E284", {"start": v(-49.36, -86.89) * mm, "end": v(-58.5, -86.89) * mm});
            skFitSpline(sketch, "E285", {"points": [v(-48.18, -60.72) * mm, v(-48.18, -60.17) * mm, v(-47.65, -59.73) * mm, v(-47, -59.73) * mm]});
            skLineSegment(sketch, "E286", {"start": v(-48.18, -85.9) * mm, "end": v(-48.18, -75.72) * mm});
            skLineSegment(sketch, "E287", {"start": v(-48.18, -75.72) * mm, "end": v(-48.18, -73.37) * mm});
            skLineSegment(sketch, "E288", {"start": v(-48.18, -73.37) * mm, "end": v(-48.18, -60.72) * mm});
            skLineSegment(sketch, "E289", {"start": v(-48.18, -60.72) * mm, "end": v(-48.18, -85.9) * mm});
            skFitSpline(sketch, "E290", {"points": [v(-46.66, -59.73) * mm, v(-46, -59.73) * mm, v(-45.48, -60.17) * mm, v(-45.48, -60.72) * mm]});
            skLineSegment(sketch, "E291", {"start": v(-47, -59.73) * mm, "end": v(-46.66, -59.73) * mm});
            skLineSegment(sketch, "E292", {"start": v(-46.66, -59.73) * mm, "end": v(-47, -59.73) * mm});
            skFitSpline(sketch, "E293", {"points": [v(-59.3, -74.84) * mm, v(-59.3, -74.28) * mm, v(-58.85, -73.84) * mm, v(-58.3, -73.84) * mm]});
            skLineSegment(sketch, "E294", {"start": v(-45.48, -60.72) * mm, "end": v(-45.48, -79.6) * mm});
            skLineSegment(sketch, "E295", {"start": v(-45.48, -79.6) * mm, "end": v(-45.48, -88.54) * mm});
            skLineSegment(sketch, "E296", {"start": v(-45.48, -88.54) * mm, "end": v(-45.48, -60.72) * mm});
            skFitSpline(sketch, "E297", {"points": [v(-52.53, -73.84) * mm, v(-51.98, -73.84) * mm, v(-51.53, -74.28) * mm, v(-51.53, -74.84) * mm]});
            skLineSegment(sketch, "E298", {"start": v(-58.3, -73.84) * mm, "end": v(-52.53, -73.84) * mm});
            skLineSegment(sketch, "E299", {"start": v(-52.53, -73.84) * mm, "end": v(-58.3, -73.84) * mm});
            skFitSpline(sketch, "E300", {"points": [v(-51.53, -80.8) * mm, v(-51.53, -81.35) * mm, v(-51.98, -81.8) * mm, v(-52.53, -81.8) * mm]});
            skLineSegment(sketch, "E301", {"start": v(-51.53, -74.84) * mm, "end": v(-51.53, -80.8) * mm});
            skLineSegment(sketch, "E302", {"start": v(-51.53, -80.8) * mm, "end": v(-51.53, -74.84) * mm});
            skFitSpline(sketch, "E303", {"points": [v(-58.3, -81.8) * mm, v(-58.85, -81.8) * mm, v(-59.3, -81.35) * mm, v(-59.3, -80.8) * mm]});
            skLineSegment(sketch, "E304", {"start": v(-52.53, -81.8) * mm, "end": v(-58.3, -81.8) * mm});
            skLineSegment(sketch, "E305", {"start": v(-58.3, -81.8) * mm, "end": v(-52.53, -81.8) * mm});
            skFitSpline(sketch, "E306", {"points": [v(-59.3, -60.73) * mm, v(-59.3, -60.17) * mm, v(-58.85, -59.73) * mm, v(-58.3, -59.73) * mm]});
            skLineSegment(sketch, "E307", {"start": v(-59.3, -80.8) * mm, "end": v(-59.3, -74.84) * mm});
            skLineSegment(sketch, "E308", {"start": v(-59.3, -74.84) * mm, "end": v(-59.3, -80.8) * mm});
            skFitSpline(sketch, "E309", {"points": [v(-52.53, -59.73) * mm, v(-51.98, -59.73) * mm, v(-51.53, -60.17) * mm, v(-51.53, -60.73) * mm]});
            skLineSegment(sketch, "E310", {"start": v(-58.3, -59.73) * mm, "end": v(-52.53, -59.73) * mm});
            skLineSegment(sketch, "E311", {"start": v(-52.53, -59.73) * mm, "end": v(-58.3, -59.73) * mm});
            skFitSpline(sketch, "E312", {"points": [v(-51.53, -66.68) * mm, v(-51.53, -67.23) * mm, v(-51.98, -67.68) * mm, v(-52.53, -67.68) * mm]});
            skLineSegment(sketch, "E313", {"start": v(-51.53, -60.73) * mm, "end": v(-51.53, -66.68) * mm});
            skLineSegment(sketch, "E314", {"start": v(-51.53, -66.68) * mm, "end": v(-51.53, -60.73) * mm});
            skFitSpline(sketch, "E315", {"points": [v(-58.3, -67.68) * mm, v(-58.85, -67.68) * mm, v(-59.3, -67.23) * mm, v(-59.3, -66.68) * mm]});
            skLineSegment(sketch, "E316", {"start": v(-52.53, -67.68) * mm, "end": v(-58.3, -67.68) * mm});
            skLineSegment(sketch, "E317", {"start": v(-58.3, -67.68) * mm, "end": v(-52.53, -67.68) * mm});
            skLineSegment(sketch, "E318", {"start": v(-59.3, -66.68) * mm, "end": v(-59.3, -60.73) * mm});
            skLineSegment(sketch, "E319", {"start": v(-59.3, -60.73) * mm, "end": v(-59.3, -66.68) * mm});
            skFitSpline(sketch, "E320", {"points": [v(-39.83, -16.28) * mm, v(-39.83, -15.72) * mm, v(-40.28, -15.27) * mm, v(-40.84, -15.27) * mm]});
            skLineSegment(sketch, "E321", {"start": v(-39.83, -41.73) * mm, "end": v(-39.83, -16.28) * mm});
            skLineSegment(sketch, "E322", {"start": v(-39.83, -16.28) * mm, "end": v(-39.83, -41.73) * mm});
            skFitSpline(sketch, "E323", {"points": [v(-58.28, -15.27) * mm, v(-58.84, -15.27) * mm, v(-59.3, -15.72) * mm, v(-59.3, -16.28) * mm]});
            skLineSegment(sketch, "E324", {"start": v(-40.84, -15.27) * mm, "end": v(-58.28, -15.27) * mm});
            skLineSegment(sketch, "E325", {"start": v(-58.28, -15.27) * mm, "end": v(-40.84, -15.27) * mm});
            skFitSpline(sketch, "E326", {"points": [v(-59.3, -53.08) * mm, v(-59.3, -53.63) * mm, v(-58.84, -54.08) * mm, v(-58.28, -54.08) * mm]});
            skLineSegment(sketch, "E327", {"start": v(-59.3, -16.28) * mm, "end": v(-59.3, -53.08) * mm});
            skLineSegment(sketch, "E328", {"start": v(-59.3, -53.08) * mm, "end": v(-59.3, -16.28) * mm});
            skFitSpline(sketch, "E329", {"points": [v(-45.71, -54.08) * mm, v(-45.71, -50.77) * mm, v(-43.08, -48.08) * mm, v(-39.83, -48.08) * mm]});
            skLineSegment(sketch, "E330", {"start": v(-58.28, -54.08) * mm, "end": v(-51.74, -54.08) * mm});
            skLineSegment(sketch, "E331", {"start": v(-51.74, -54.08) * mm, "end": v(-45.71, -54.08) * mm});
            skLineSegment(sketch, "E332", {"start": v(-45.71, -54.08) * mm, "end": v(-58.28, -54.08) * mm});
            skLineSegment(sketch, "E333", {"start": v(-39.83, -48.08) * mm, "end": v(-39.83, -41.73) * mm});
            skLineSegment(sketch, "E334", {"start": v(-39.83, -41.73) * mm, "end": v(-39.83, -48.08) * mm});
            skFitSpline(sketch, "E335", {"points": [v(-31.53, -118.22) * mm, v(-31.53, -118.77) * mm, v(-31.04, -119.22) * mm, v(-30.44, -119.22) * mm]});
            skLineSegment(sketch, "E336", {"start": v(-31.53, -111.58) * mm, "end": v(-31.53, -118.22) * mm});
            skLineSegment(sketch, "E337", {"start": v(-31.53, -118.22) * mm, "end": v(-31.53, -111.58) * mm});
            skFitSpline(sketch, "E338", {"points": [v(-12.84, -119.22) * mm, v(-12.24, -119.22) * mm, v(-11.75, -118.77) * mm, v(-11.75, -118.22) * mm]});
            skLineSegment(sketch, "E339", {"start": v(-30.44, -119.22) * mm, "end": v(-12.84, -119.22) * mm});
            skLineSegment(sketch, "E340", {"start": v(-12.84, -119.22) * mm, "end": v(-30.44, -119.22) * mm});
            skFitSpline(sketch, "E341", {"points": [v(-11.75, -97.17) * mm, v(-11.75, -96.62) * mm, v(-12.24, -96.17) * mm, v(-12.84, -96.17) * mm]});
            skLineSegment(sketch, "E342", {"start": v(-11.75, -118.22) * mm, "end": v(-11.75, -97.17) * mm});
            skLineSegment(sketch, "E343", {"start": v(-11.75, -97.17) * mm, "end": v(-11.75, -118.22) * mm});
            skFitSpline(sketch, "E344", {"points": [v(-25.53, -96.17) * mm, v(-25.53, -99.49) * mm, v(-28.22, -102.17) * mm, v(-31.53, -102.17) * mm]});
            skLineSegment(sketch, "E345", {"start": v(-12.84, -96.17) * mm, "end": v(-19.6, -96.17) * mm});
            skLineSegment(sketch, "E346", {"start": v(-19.6, -96.17) * mm, "end": v(-25.53, -96.17) * mm});
            skLineSegment(sketch, "E347", {"start": v(-25.53, -96.17) * mm, "end": v(-12.84, -96.17) * mm});
            skLineSegment(sketch, "E348", {"start": v(-31.53, -102.17) * mm, "end": v(-31.53, -111.58) * mm});
            skLineSegment(sketch, "E349", {"start": v(-31.53, -111.58) * mm, "end": v(-31.53, -102.17) * mm});
            skFitSpline(sketch, "E350", {"points": [v(-57.9, -119.22) * mm, v(-58.67, -119.22) * mm, v(-59.3, -118.74) * mm, v(-59.3, -118.16) * mm]});
            skLineSegment(sketch, "E351", {"start": v(-35.49, -119.22) * mm, "end": v(-57.9, -119.22) * mm});
            skFitSpline(sketch, "E352", {"points": [v(-59.3, -103.23) * mm, v(-59.3, -102.65) * mm, v(-58.67, -102.17) * mm, v(-57.9, -102.17) * mm]});
            skLineSegment(sketch, "E353", {"start": v(-59.3, -118.16) * mm, "end": v(-59.3, -103.23) * mm});
            skLineSegment(sketch, "E354", {"start": v(-57.9, -102.17) * mm, "end": v(-35.49, -102.17) * mm});
            skFitSpline(sketch, "E355", {"points": [v(-12.75, -48.08) * mm, v(-12.2, -48.08) * mm, v(-11.75, -47.63) * mm, v(-11.75, -47.08) * mm]});
            skLineSegment(sketch, "E356", {"start": v(-35.49, -48.08) * mm, "end": v(-12.75, -48.08) * mm});
            skFitSpline(sketch, "E357", {"points": [v(-11.75, -16.28) * mm, v(-11.75, -15.72) * mm, v(-12.2, -15.27) * mm, v(-12.75, -15.27) * mm]});
            skLineSegment(sketch, "E358", {"start": v(-11.75, -47.08) * mm, "end": v(-11.75, -16.28) * mm});
            skFitSpline(sketch, "E359", {"points": [v(-11.75, 16.06) * mm, v(-11.75, 15.67) * mm, v(-12.2, 15.36) * mm, v(-12.75, 15.36) * mm]});
            skLineSegment(sketch, "E360", {"start": v(-12.75, -15.27) * mm, "end": v(-35.49, -15.27) * mm});
            skFitSpline(sketch, "E361", {"points": [v(-18.04, 15.36) * mm, v(-18.6, 15.36) * mm, v(-19.04, 15.67) * mm, v(-19.04, 16.06) * mm]});
            skLineSegment(sketch, "E362", {"start": v(-12.75, 15.36) * mm, "end": v(-18.04, 15.36) * mm});
            skLineSegment(sketch, "E363", {"start": v(-18.04, 15.36) * mm, "end": v(-12.75, 15.36) * mm});
            skFitSpline(sketch, "E364", {"points": [v(-19.04, 37.7) * mm, v(-19.04, 38.1) * mm, v(-18.6, 38.4) * mm, v(-18.04, 38.4) * mm]});
            skLineSegment(sketch, "E365", {"start": v(-19.04, 16.06) * mm, "end": v(-19.04, 37.7) * mm});
            skLineSegment(sketch, "E366", {"start": v(-19.04, 37.7) * mm, "end": v(-19.04, 16.06) * mm});
            skFitSpline(sketch, "E367", {"points": [v(-12.75, 38.4) * mm, v(-12.2, 38.4) * mm, v(-11.75, 38.1) * mm, v(-11.75, 37.7) * mm]});
            skLineSegment(sketch, "E368", {"start": v(-18.04, 38.4) * mm, "end": v(-12.75, 38.4) * mm});
            skLineSegment(sketch, "E369", {"start": v(-12.75, 38.4) * mm, "end": v(-18.04, 38.4) * mm});
            skFitSpline(sketch, "E370", {"points": [v(-11.75, 87.5) * mm, v(-11.75, 86.95) * mm, v(-12.2, 86.5) * mm, v(-12.75, 86.5) * mm]});
            skLineSegment(sketch, "E371", {"start": v(-11.75, 37.7) * mm, "end": v(-11.75, 16.06) * mm});
            skLineSegment(sketch, "E372", {"start": v(-11.75, 16.06) * mm, "end": v(-11.75, 37.7) * mm});
            skFitSpline(sketch, "E373", {"points": [v(-18.04, 86.5) * mm, v(-18.6, 86.5) * mm, v(-19.04, 86.95) * mm, v(-19.04, 87.5) * mm]});
            skLineSegment(sketch, "E374", {"start": v(-12.75, 86.5) * mm, "end": v(-18.04, 86.5) * mm});
            skLineSegment(sketch, "E375", {"start": v(-18.04, 86.5) * mm, "end": v(-12.75, 86.5) * mm});
            skFitSpline(sketch, "E376", {"points": [v(-19.04, 118.3) * mm, v(-19.04, 118.85) * mm, v(-18.6, 119.3) * mm, v(-18.04, 119.3) * mm]});
            skLineSegment(sketch, "E377", {"start": v(-19.04, 87.5) * mm, "end": v(-19.04, 118.3) * mm});
            skLineSegment(sketch, "E378", {"start": v(-19.04, 118.3) * mm, "end": v(-19.04, 87.5) * mm});
            skFitSpline(sketch, "E379", {"points": [v(-12.75, 119.3) * mm, v(-12.2, 119.3) * mm, v(-11.75, 118.85) * mm, v(-11.75, 118.3) * mm]});
            skLineSegment(sketch, "E380", {"start": v(-18.04, 119.3) * mm, "end": v(-12.75, 119.3) * mm});
            skLineSegment(sketch, "E381", {"start": v(-12.75, 119.3) * mm, "end": v(-18.04, 119.3) * mm});
            skFitSpline(sketch, "E382", {"points": [v(63.9, -124.73) * mm, v(63.9, -127.03) * mm, v(62, -128.9) * mm, v(59.65, -128.9) * mm]});
            skLineSegment(sketch, "E383", {"start": v(-11.75, 118.3) * mm, "end": v(-11.75, 87.5) * mm});
            skFitSpline(sketch, "E384", {"points": [v(12, -128.9) * mm, v(9.66, -128.9) * mm, v(7.76, -127.03) * mm, v(7.76, -124.73) * mm]});
            skLineSegment(sketch, "E385", {"start": v(59.65, -128.9) * mm, "end": v(12, -128.9) * mm});
            skLineSegment(sketch, "E386", {"start": v(12, -128.9) * mm, "end": v(59.65, -128.9) * mm});
            skFitSpline(sketch, "E387", {"points": [v(7.76, -10.2) * mm, v(7.76, -7.9) * mm, v(9.66, -6.03) * mm, v(12, -6.03) * mm]});
            skLineSegment(sketch, "E388", {"start": v(7.76, -124.73) * mm, "end": v(7.76, -10.2) * mm});
            skLineSegment(sketch, "E389", {"start": v(7.76, -10.2) * mm, "end": v(7.76, -124.73) * mm});
            skFitSpline(sketch, "E390", {"points": [v(59.65, -6.03) * mm, v(62, -6.03) * mm, v(63.9, -7.9) * mm, v(63.9, -10.2) * mm]});
            skLineSegment(sketch, "E391", {"start": v(12, -6.03) * mm, "end": v(59.65, -6.03) * mm});
            skLineSegment(sketch, "E392", {"start": v(59.65, -6.03) * mm, "end": v(12, -6.03) * mm});
            skFitSpline(sketch, "E393", {"points": [v(59.57, -76.2) * mm, v(59.57, -76.75) * mm, v(59.12, -77.2) * mm, v(58.57, -77.2) * mm]});
            skLineSegment(sketch, "E394", {"start": v(63.9, -10.2) * mm, "end": v(63.9, -124.73) * mm});
            skLineSegment(sketch, "E395", {"start": v(63.9, -124.73) * mm, "end": v(63.9, -10.2) * mm});
            skFitSpline(sketch, "E396", {"points": [v(52.8, -77.2) * mm, v(52.26, -77.2) * mm, v(51.8, -76.75) * mm, v(51.8, -76.2) * mm]});
            skLineSegment(sketch, "E397", {"start": v(58.57, -77.2) * mm, "end": v(52.8, -77.2) * mm});
            skLineSegment(sketch, "E398", {"start": v(52.8, -77.2) * mm, "end": v(58.57, -77.2) * mm});
            skFitSpline(sketch, "E399", {"points": [v(51.8, -70.24) * mm, v(51.8, -69.69) * mm, v(52.26, -69.24) * mm, v(52.8, -69.24) * mm]});
            skLineSegment(sketch, "E400", {"start": v(51.8, -76.2) * mm, "end": v(51.8, -70.24) * mm});
            skLineSegment(sketch, "E401", {"start": v(51.8, -70.24) * mm, "end": v(51.8, -76.2) * mm});
            skFitSpline(sketch, "E402", {"points": [v(58.57, -69.24) * mm, v(59.12, -69.24) * mm, v(59.57, -69.69) * mm, v(59.57, -70.24) * mm]});
            skLineSegment(sketch, "E403", {"start": v(52.8, -69.24) * mm, "end": v(58.57, -69.24) * mm});
            skLineSegment(sketch, "E404", {"start": v(58.57, -69.24) * mm, "end": v(52.8, -69.24) * mm});
            skFitSpline(sketch, "E405", {"points": [v(59.57, -90.3) * mm, v(59.57, -90.86) * mm, v(59.12, -91.3) * mm, v(58.57, -91.3) * mm]});
            skLineSegment(sketch, "E406", {"start": v(59.57, -70.24) * mm, "end": v(59.57, -76.2) * mm});
            skLineSegment(sketch, "E407", {"start": v(59.57, -76.2) * mm, "end": v(59.57, -70.24) * mm});
            skFitSpline(sketch, "E408", {"points": [v(52.8, -91.3) * mm, v(52.26, -91.3) * mm, v(51.8, -90.86) * mm, v(51.8, -90.3) * mm]});
            skLineSegment(sketch, "E409", {"start": v(58.57, -91.3) * mm, "end": v(52.8, -91.3) * mm});
            skLineSegment(sketch, "E410", {"start": v(52.8, -91.3) * mm, "end": v(58.57, -91.3) * mm});
            skFitSpline(sketch, "E411", {"points": [v(51.8, -84.35) * mm, v(51.8, -83.8) * mm, v(52.26, -83.35) * mm, v(52.8, -83.35) * mm]});
            skLineSegment(sketch, "E412", {"start": v(51.8, -90.3) * mm, "end": v(51.8, -84.35) * mm});
            skLineSegment(sketch, "E413", {"start": v(51.8, -84.35) * mm, "end": v(51.8, -90.3) * mm});
            skFitSpline(sketch, "E414", {"points": [v(58.57, -83.35) * mm, v(59.12, -83.35) * mm, v(59.57, -83.8) * mm, v(59.57, -84.35) * mm]});
            skLineSegment(sketch, "E415", {"start": v(52.8, -83.35) * mm, "end": v(58.57, -83.35) * mm});
            skLineSegment(sketch, "E416", {"start": v(58.57, -83.35) * mm, "end": v(52.8, -83.35) * mm});
            skFitSpline(sketch, "E417", {"points": [v(59.57, -118.51) * mm, v(59.57, -118.9) * mm, v(59.12, -119.22) * mm, v(58.57, -119.22) * mm]});
            skLineSegment(sketch, "E418", {"start": v(59.57, -84.35) * mm, "end": v(59.57, -90.3) * mm});
            skLineSegment(sketch, "E419", {"start": v(59.57, -90.3) * mm, "end": v(59.57, -84.35) * mm});
            skFitSpline(sketch, "E420", {"points": [v(53.28, -119.22) * mm, v(52.73, -119.22) * mm, v(52.28, -118.9) * mm, v(52.28, -118.51) * mm]});
            skLineSegment(sketch, "E421", {"start": v(58.57, -119.22) * mm, "end": v(53.28, -119.22) * mm});
            skLineSegment(sketch, "E422", {"start": v(53.28, -119.22) * mm, "end": v(58.57, -119.22) * mm});
            skFitSpline(sketch, "E423", {"points": [v(52.28, -96.88) * mm, v(52.28, -96.49) * mm, v(52.73, -96.17) * mm, v(53.28, -96.17) * mm]});
            skLineSegment(sketch, "E424", {"start": v(52.28, -118.51) * mm, "end": v(52.28, -96.88) * mm});
            skLineSegment(sketch, "E425", {"start": v(52.28, -96.88) * mm, "end": v(52.28, -118.51) * mm});
            skFitSpline(sketch, "E426", {"points": [v(58.57, -96.17) * mm, v(59.12, -96.17) * mm, v(59.57, -96.49) * mm, v(59.57, -96.88) * mm]});
            skLineSegment(sketch, "E427", {"start": v(53.28, -96.17) * mm, "end": v(58.57, -96.17) * mm});
            skLineSegment(sketch, "E428", {"start": v(58.57, -96.17) * mm, "end": v(53.28, -96.17) * mm});
            skFitSpline(sketch, "E429", {"points": [v(59.57, -47.08) * mm, v(59.57, -47.63) * mm, v(59.12, -48.08) * mm, v(58.57, -48.08) * mm]});
            skLineSegment(sketch, "E430", {"start": v(59.57, -96.88) * mm, "end": v(59.57, -118.51) * mm});
            skLineSegment(sketch, "E431", {"start": v(59.57, -118.51) * mm, "end": v(59.57, -96.88) * mm});
            skFitSpline(sketch, "E432", {"points": [v(53.28, -48.08) * mm, v(52.73, -48.08) * mm, v(52.28, -47.63) * mm, v(52.28, -47.08) * mm]});
            skLineSegment(sketch, "E433", {"start": v(58.57, -48.08) * mm, "end": v(53.28, -48.08) * mm});
            skLineSegment(sketch, "E434", {"start": v(53.28, -48.08) * mm, "end": v(58.57, -48.08) * mm});
            skFitSpline(sketch, "E435", {"points": [v(52.28, -16.28) * mm, v(52.28, -15.72) * mm, v(52.73, -15.28) * mm, v(53.28, -15.28) * mm]});
            skLineSegment(sketch, "E436", {"start": v(52.28, -47.08) * mm, "end": v(52.28, -16.28) * mm});
            skLineSegment(sketch, "E437", {"start": v(52.28, -16.28) * mm, "end": v(52.28, -47.08) * mm});
            skFitSpline(sketch, "E438", {"points": [v(58.57, -15.28) * mm, v(59.12, -15.28) * mm, v(59.57, -15.72) * mm, v(59.57, -16.28) * mm]});
            skLineSegment(sketch, "E439", {"start": v(53.28, -15.28) * mm, "end": v(58.57, -15.28) * mm});
            skLineSegment(sketch, "E440", {"start": v(58.57, -15.28) * mm, "end": v(53.28, -15.28) * mm});
            skLineSegment(sketch, "E441", {"start": v(59.57, -16.28) * mm, "end": v(59.57, -47.08) * mm});
            skLineSegment(sketch, "E442", {"start": v(59.57, -47.08) * mm, "end": v(59.57, -16.28) * mm});
            skLineSegment(sketch, "E443", {"start": v(70.9, -135.2) * mm, "end": v(-70.9, -135.2) * mm});
            skLineSegment(sketch, "E444", {"start": v(-70.9, -135.2) * mm, "end": v(-70.9, 135.2) * mm});
            skLineSegment(sketch, "E445", {"start": v(-70.9, 135.2) * mm, "end": v(70.9, 135.2) * mm});
            skLineSegment(sketch, "E446", {"start": v(70.9, 135.2) * mm, "end": v(70.9, -135.2) * mm});
            skSolve(sketch);
        }
        {
            var Q0;
            Q0=makeQuery(id+"F0.imprint","IMPRINT",FACE,{"disambiguationData":[TD([[makeQuery(id+"F0.imprint","IMPRINT",EDGE,{"derivedFrom":sQuery(id+"F0.wireOp",EDGE,"E10")}),1.0]])]});
            extrude(context, id + "F1", {"entities" : qUnion([Q0]), "depth" : 3 * mm});
        }
        {
            var Q0;
            {var subQ0=sQuery(id+"F0.wireOp",EDGE,"E0");Q0=makeQuery(id+"F0.imprint","IMPRINT",FACE,{"disambiguationData":[TD([[makeQuery(id+"F0.imprint","IMPRINT",EDGE,{"derivedFrom":subQ0}),1.0]])]});}
            extrude(context, id + "F2", {"entities" : qUnion([Q0]), "operationType" : NewBodyOperationType.ADD, "depth" : 5 * mm});
        }
        {
            var Q0;
            {var subQ26=sQuery(id+"F0.wireOp",EDGE,"E0");Q0=makeQuery(id+"F0.imprint","IMPRINT",FACE,{"disambiguationData":[TD([[makeQuery(id+"F0.imprint","IMPRINT",EDGE,{"derivedFrom":subQ26}),-1.0]])]});}
            var Q1;
            {var subQ1=sQuery(id+"F0.wireOp",EDGE,"E194");Q1=makeQuery(id+"F0.imprint","IMPRINT",FACE,{"disambiguationData":[TD([[makeQuery(id+"F0.imprint","IMPRINT",EDGE,{"derivedFrom":subQ1}),1.0]])]});}
            var Q2;
            Q2=makeQuery(id+"F0.imprint","IMPRINT",FACE,{"disambiguationData":[TD([[makeQuery(id+"F0.imprint","IMPRINT",EDGE,{"derivedFrom":sQuery(id+"F0.wireOp",EDGE,"E158")}),1.0]])]});
            var Q3;
            {var subQ2=sQuery(id+"F0.wireOp",EDGE,"E49");Q3=makeQuery(id+"F0.imprint","IMPRINT",FACE,{"disambiguationData":[TD([[makeQuery(id+"F0.imprint","IMPRINT",EDGE,{"derivedFrom":subQ2}),-1.0]])]});}
            var Q4;
            Q4=makeQuery(id+"F0.imprint","IMPRINT",FACE,{"disambiguationData":[TD([[makeQuery(id+"F0.imprint","IMPRINT",EDGE,{"derivedFrom":sQuery(id+"F0.wireOp",EDGE,"E188")}),-1.0]])]});
            var Q5;
            {var subQ1=sQuery(id+"F0.wireOp",EDGE,"E173");Q5=makeQuery(id+"F0.imprint","IMPRINT",FACE,{"disambiguationData":[TD([[makeQuery(id+"F0.imprint","IMPRINT",EDGE,{"derivedFrom":subQ1}),1.0]])]});}
            var Q6;
            Q6=makeQuery(id+"F0.imprint","IMPRINT",FACE,{"disambiguationData":[TD([[makeQuery(id+"F0.imprint","IMPRINT",EDGE,{"derivedFrom":sQuery(id+"F0.wireOp",EDGE,"E62")}),-1.0]])]});
            var Q7;
            Q7=makeQuery(id+"F0.imprint","IMPRINT",FACE,{"disambiguationData":[TD([[makeQuery(id+"F0.imprint","IMPRINT",EDGE,{"derivedFrom":sQuery(id+"F0.wireOp",EDGE,"E110")}),-1.0]])]});
            var Q8;
            Q8=makeQuery(id+"F0.imprint","IMPRINT",FACE,{"disambiguationData":[TD([[makeQuery(id+"F0.imprint","IMPRINT",EDGE,{"derivedFrom":sQuery(id+"F0.wireOp",EDGE,"E131")}),-1.0]])]});
            var Q9;
            Q9=makeQuery(id+"F0.imprint","IMPRINT",FACE,{"disambiguationData":[TD([[makeQuery(id+"F0.imprint","IMPRINT",EDGE,{"derivedFrom":sQuery(id+"F0.wireOp",EDGE,"E144")}),-1.0]])]});
            extrude(context, id + "F3", {"entities" : qUnion([Q0, Q1, Q2, Q3, Q4, Q5, Q6, Q7, Q8, Q9]), "operationType" : NewBodyOperationType.ADD, "depth" : 5 * mm});
        }
        {
            var Q0;
            Q0=makeQuery(id+"F0.imprint","IMPRINT",FACE,{"disambiguationData":[TD([[makeQuery(id+"F0.imprint","IMPRINT",EDGE,{"derivedFrom":sQuery(id+"F0.wireOp",EDGE,"E373")}),-1.0]])]});
            var Q1;
            Q1=makeQuery(id+"F0.imprint","IMPRINT",FACE,{"disambiguationData":[TD([[makeQuery(id+"F0.imprint","IMPRINT",EDGE,{"derivedFrom":sQuery(id+"F0.wireOp",EDGE,"E83")}),-1.0]])]});
            var Q2;
            Q2=makeQuery(id+"F0.imprint","IMPRINT",FACE,{"disambiguationData":[TD([[makeQuery(id+"F0.imprint","IMPRINT",EDGE,{"derivedFrom":sQuery(id+"F0.wireOp",EDGE,"E96")}),-1.0]])]});
            var Q3;
            {var subQ9=sQuery(id+"F0.wireOp",EDGE,"E176");Q3=makeQuery(id+"F0.imprint","IMPRINT",FACE,{"disambiguationData":[TD([[makeQuery(id+"F0.imprint","IMPRINT",EDGE,{"derivedFrom":subQ9}),1.0]])]});}
            extrude(context, id + "F4", {"entities" : qUnion([Q0, Q1, Q2, Q3]), "depth" : 3 * mm});
        }
        {
            var Q0;
            {var subQ26=sQuery(id+"F0.wireOp",EDGE,"E0");Q0=makeQuery(id+"F0.imprint","IMPRINT",FACE,{"disambiguationData":[TD([[makeQuery(id+"F0.imprint","IMPRINT",EDGE,{"derivedFrom":subQ26}),-1.0]])]});}
            extrude(context, id + "F5", {"entities" : qUnion([Q0]), "depth" : 7 * mm});
        }
    });
